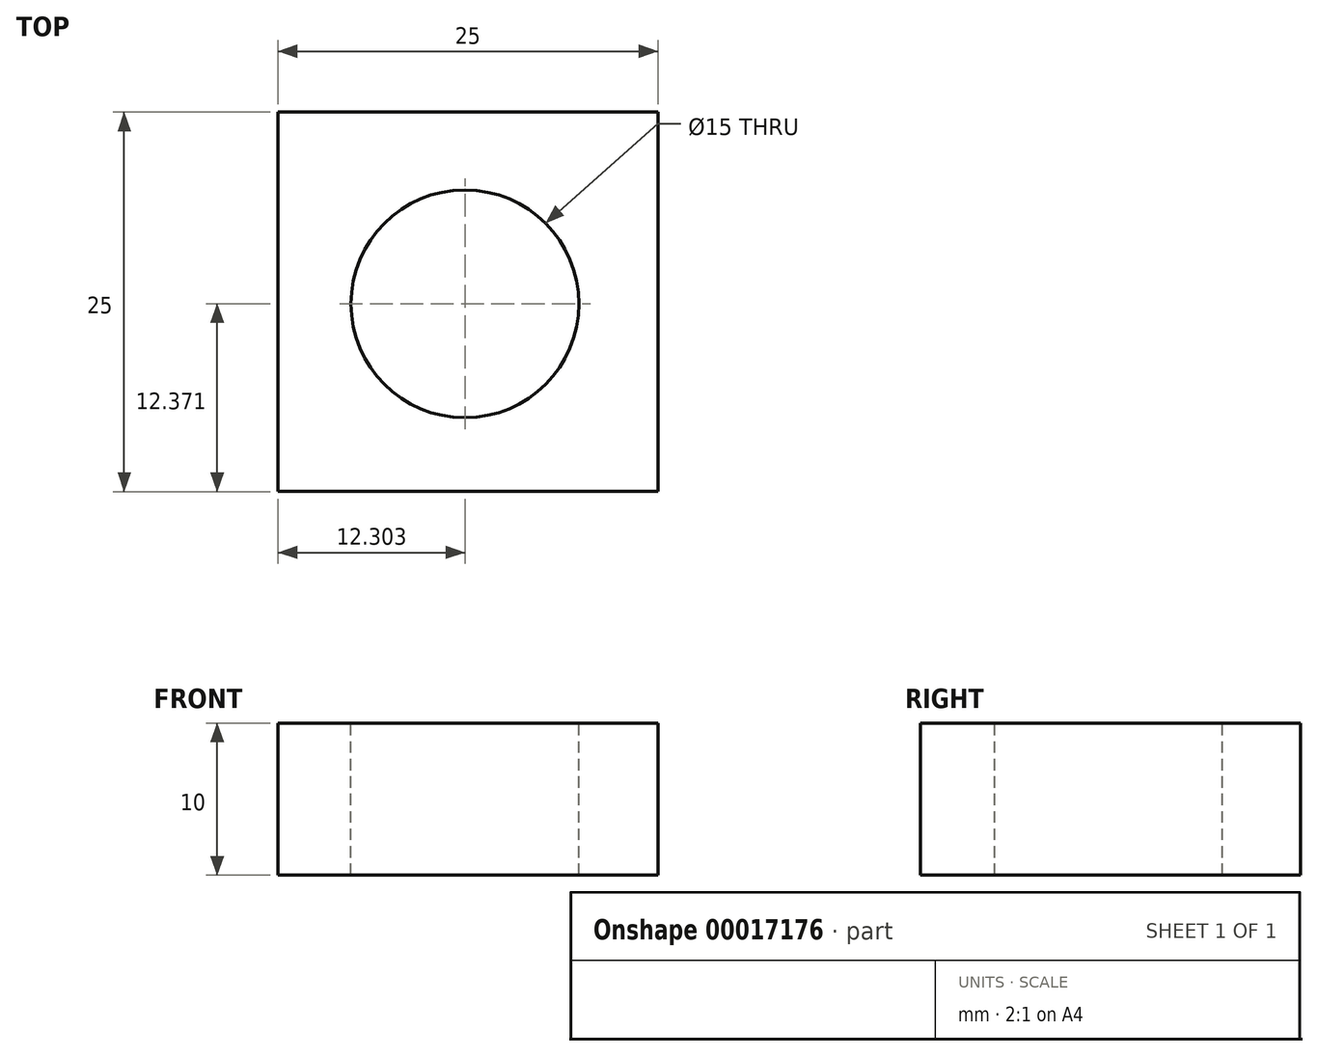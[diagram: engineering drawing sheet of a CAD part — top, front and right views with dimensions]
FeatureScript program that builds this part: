
annotation { "Feature Type Name" : "Feature", "Feature Type Description" : "" }
export const myFeature = defineFeature(function(context is Context, id is Id, definition is map)
    precondition{}
    {
        {
            var Q0;
            Q0=qCreatedBy(makeId("Top.planeOp"),FACE);
            var sketch = newSketch(context, id + "F0", { "sketchPlane" : qUnion([Q0])});
            skLineSegment(sketch, "E0.bottom", {"start": v(-16.53, 9.97) * mm, "end": v(8.47, 9.97) * mm});
            skLineSegment(sketch, "E0.top", {"start": v(-16.53, -15.03) * mm, "end": v(8.47, -15.03) * mm});
            skLineSegment(sketch, "E0.left", {"start": v(-16.53, 9.97) * mm, "end": v(-16.53, -15.03) * mm});
            skLineSegment(sketch, "E0.right", {"start": v(8.47, 9.97) * mm, "end": v(8.47, -15.03) * mm});
            skSolve(sketch);
        }
        {
            var Q0;
            Q0 = qSketchRegion(id + "F0", true);
            extrude(context, id + "F1", {"entities" : qUnion([Q0]), "depth" : 10 * mm});
        }
        {
            var Q0;
            Q0=makeQuery(id+"F1.opExtrude","CAP_FACE",FACE,{"disambiguationData":[OSD([sQuery(id+"F0.wireOp",EDGE,"E0.bottom"),sQuery(id+"F0.wireOp",EDGE,"E0.top"),sQuery(id+"F0.wireOp",EDGE,"E0.left"),sQuery(id+"F0.wireOp",EDGE,"E0.right")])],"isStart":false});
            var sketch = newSketch(context, id + "F2", { "sketchPlane" : qUnion([Q0])});
            skCircle(sketch, "E1", {"center": v(-4.23, -2.66) * mm, "radius": 7.97 * mm});
            skSolve(sketch);
        }
        {
            var Q0;
            Q0=sQuery(id+"F2.wireOp",VERTEX,"E1.center");
            var Q1;
            Q1=makeQuery(id+"F1.opExtrude","SWEPT_BODY",BODY,{"disambiguationData":[OSD([sQuery(id+"F0.wireOp",EDGE,"E0.bottom"),sQuery(id+"F0.wireOp",EDGE,"E0.top"),sQuery(id+"F0.wireOp",EDGE,"E0.left"),sQuery(id+"F0.wireOp",EDGE,"E0.right")])]});
            hole(context, id + "F3", {"style" : HoleStyle.SIMPLE, "holeDiameter" : 15 * mm, "endStyle" : HoleEndStyle.THROUGH, "locations" : qUnion([Q0]), "scope" : qUnion([Q1])});
        }
    });
